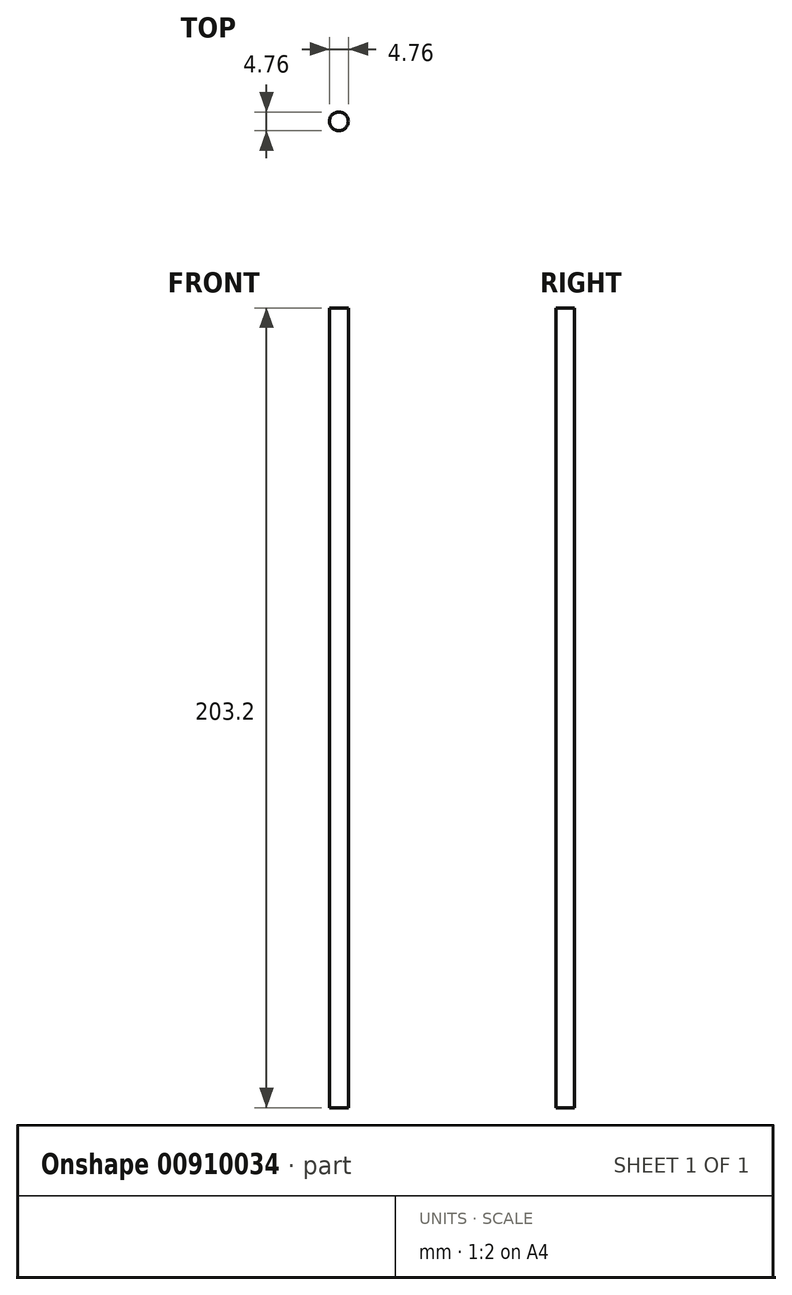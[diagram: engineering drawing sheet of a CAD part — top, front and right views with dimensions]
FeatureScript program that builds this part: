
annotation { "Feature Type Name" : "Feature", "Feature Type Description" : "" }
export const myFeature = defineFeature(function(context is Context, id is Id, definition is map)
    precondition{}
    {
        {
            var Q0;
            Q0=qCreatedBy(makeId("Top.planeOp"),FACE);
            var sketch = newSketch(context, id + "F0", { "sketchPlane" : qUnion([Q0])});
            skCircle(sketch, "E0", {"center": v(0, 0) * mm, "radius": 2.38 * mm});
            skSolve(sketch);
        }
        {
            var Q0;
            Q0 = qSketchRegion(id + "F0", true);
            extrude(context, id + "F1", {"entities" : qUnion([Q0]), "endBound" : BoundingType.SYMMETRIC, "depth" : 203.2 * mm, "offsetDistance" : 25.4 * mm});
        }
    });
